# Revit family: EKF_EE_СейсмокомплектДляШкафаTrivia_AVERES
name_source: partatom
category: Электрооборудование
units: mm (PartAtom-declared; Revit-internal decimal feet)

## family parameters
Всегда вертикально = Нет
На основе рабочей плоскости = Да
Общий = Да
При загрузке вырезать с полостями = Нет
Размер круглого соединителя = Использовать диаметр
Тип детали = Силовой щит
Точка расчета площади = Нет

## types (2) — shared parameters
ADSK_Единица измерения = шт.
ADSK_Завод-изготовитель = EKF
ADSK_Количество = 1
ВерхняяГраньНижнихПанелей = 130 мм
ВнОтверстия = 75 мм
ВысотаПанели = 130 мм
Изготовитель = EKF
ОсевыеКронштейнов = 125 мм
Отметка по умолчанию = 1219.2 мм
Серия номенклатуры = Averes
Степень защиты IP = -
ТВ = EKF_2_TRIVIA_AVERES
Тип установки = -
вСветуМеждуПанелями = 1700 мм
zero-valued in all types: ADSK_Масса, ADSK_Размер_Высота, ADSK_Размер_Глубина

## per-type parameters (varying)
| type | ADSK_Код изделия | ADSK_Размер_Ширина | Верх_Низ | Тип | ШиринаПанелей | ШиринаУстановкиКронштейнов |
| Сейсмокомплект для шкафа Ш600 EKF AVERES | ASK600 | 600 мм | Вл_EKF_EE_ASK600_ASK800_Панели : Панели Ш600 | 754 мм | 566 мм | 548 мм |
| Сейсмокомплект для шкафа Ш800 EKF AVERES | ASK800 | 800 мм | Вл_EKF_EE_ASK600_ASK800_Панели : Панели Ш800 | 755 мм | 766 мм | 748 мм |

note: column(s) folded — value = type name in every type: ADSK_Марка, ADSK_Наименование, ADSK_Обозначение
